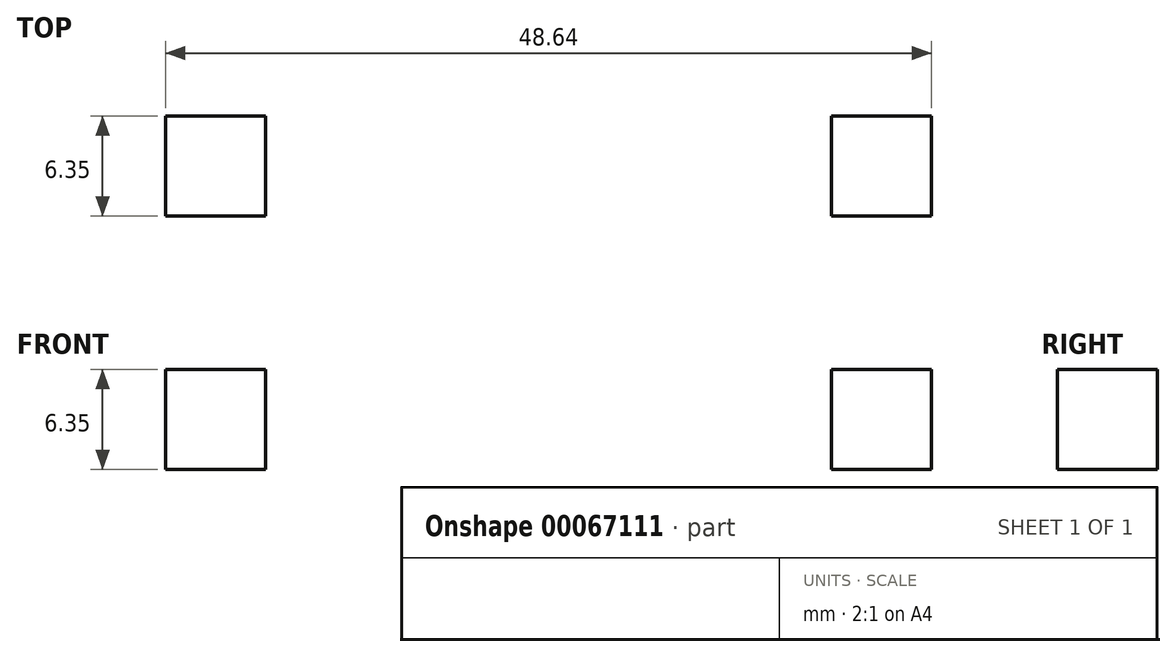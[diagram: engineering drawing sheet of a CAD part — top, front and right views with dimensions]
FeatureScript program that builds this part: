
annotation { "Feature Type Name" : "Feature", "Feature Type Description" : "" }
export const myFeature = defineFeature(function(context is Context, id is Id, definition is map)
    precondition{}
    {
        {
            var Q0;
            Q0=qCreatedBy(makeId("Top.planeOp"),FACE);
            var sketch = newSketch(context, id + "F0", { "sketchPlane" : qUnion([Q0])});
            skLineSegment(sketch, "E0.bottom", {"start": v(-24.32, 0) * mm, "end": v(24.32, 0) * mm});
            skLineSegment(sketch, "E0.top", {"start": v(-24.32, -51.82) * mm, "end": v(24.32, -51.83) * mm});
            skLineSegment(sketch, "E0.left", {"start": v(-24.32, 0) * mm, "end": v(-24.32, -51.82) * mm});
            skLineSegment(sketch, "E0.right", {"start": v(24.33, 0) * mm, "end": v(24.33, -51.82) * mm});
            skLineSegment(sketch, "E1.bottom", {"start": v(-9, -12.32) * mm, "end": v(9, -12.32) * mm});
            skLineSegment(sketch, "E1.top", {"start": v(-9, -36.32) * mm, "end": v(9, -36.32) * mm});
            skLineSegment(sketch, "E1.left", {"start": v(-9, -12.32) * mm, "end": v(-9, -36.32) * mm});
            skLineSegment(sketch, "E1.right", {"start": v(9, -12.32) * mm, "end": v(9, -36.32) * mm});
            skLineSegment(sketch, "E2", {"start": v(-9, -12.32) * mm, "end": v(-24.32, -12.32) * mm, "construction": true});
            skLineSegment(sketch, "E3", {"start": v(9, -12.32) * mm, "end": v(24.32, -12.32) * mm, "construction": true});
            skLineSegment(sketch, "E4", {"start": v(0, 0) * mm, "end": v(0, -12.32) * mm, "construction": true});
            skLineSegment(sketch, "E5.bottom", {"start": v(-24.32, 0) * mm, "end": v(-17.97, 0) * mm});
            skLineSegment(sketch, "E5.top", {"start": v(-24.33, -6.35) * mm, "end": v(-17.98, -6.35) * mm});
            skLineSegment(sketch, "E5.left", {"start": v(-24.32, 0) * mm, "end": v(-24.32, -6.35) * mm});
            skLineSegment(sketch, "E5.right", {"start": v(-17.98, 0) * mm, "end": v(-17.98, -6.35) * mm});
            skLineSegment(sketch, "E6.bottom", {"start": v(24.32, 0) * mm, "end": v(17.98, 0) * mm});
            skLineSegment(sketch, "E6.top", {"start": v(24.33, -6.35) * mm, "end": v(17.98, -6.35) * mm});
            skLineSegment(sketch, "E6.left", {"start": v(24.32, 0) * mm, "end": v(24.32, -6.35) * mm});
            skLineSegment(sketch, "E6.right", {"start": v(17.98, 0) * mm, "end": v(17.98, -6.35) * mm});
            skLineSegment(sketch, "E7.bottom", {"start": v(24.32, -51.83) * mm, "end": v(17.98, -51.83) * mm});
            skLineSegment(sketch, "E7.top", {"start": v(24.33, -45.48) * mm, "end": v(17.98, -45.48) * mm});
            skLineSegment(sketch, "E7.left", {"start": v(24.32, -51.83) * mm, "end": v(24.32, -45.48) * mm});
            skLineSegment(sketch, "E7.right", {"start": v(17.98, -51.83) * mm, "end": v(17.98, -45.48) * mm});
            skLineSegment(sketch, "E8.bottom", {"start": v(-24.32, -51.82) * mm, "end": v(-17.98, -51.82) * mm});
            skLineSegment(sketch, "E8.top", {"start": v(-24.33, -45.48) * mm, "end": v(-17.98, -45.48) * mm});
            skLineSegment(sketch, "E8.left", {"start": v(-24.32, -51.82) * mm, "end": v(-24.32, -45.48) * mm});
            skLineSegment(sketch, "E8.right", {"start": v(-17.98, -51.83) * mm, "end": v(-17.98, -45.48) * mm});
            skLineSegment(sketch, "E9", {"start": v(0, -36.32) * mm, "end": v(0, -51.83) * mm, "construction": true});
            skSolve(sketch);
        }
        {
            var Q0;
            Q0=makeQuery(id+"F0.imprint","IMPRINT",FACE,{"disambiguationData":[TD([[makeQuery(id+"F0.imprint","IMPRINT",EDGE,{"derivedFrom":sQuery(id+"F0.wireOp",EDGE,"E0.bottom")}),-1.0]])]});
            extrude(context, id + "F1", {"entities" : qUnion([Q0]), "depth" : 6.35 * mm});
        }
    });
